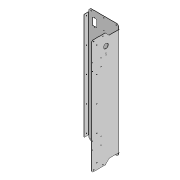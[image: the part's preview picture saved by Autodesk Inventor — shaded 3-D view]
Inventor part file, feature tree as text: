
AUTODESK INVENTOR PART (.ipt)
format: ipt  version: 2020 (Build 240168000, 168)  size: 658,944 bytes
history: native  units: mm
features: sketch x20, projected_geometry x12, other x10, hole x10, extrude x7, fillet x5, chamfer x3
ambient origin geometry x8: Origin, YZ Plane, XZ Plane, XY Plane, X Axis, Y Axis, Z Axis, Center Point
bodies: Body1 (feature_tree)
feature tree (67):
  other  "ソリッド1"
  other  "フランジ1"
  extrude  "押し出し2"  Depth=200.0mm
  hole  "穴2"  [1 undecoded]
  fillet  "フィレット1"  Radius=2.0mm
  other  "フランジ3"
  hole  "穴4"  [1 undecoded]
  hole  "穴5"  [1 undecoded]
  hole  "穴6"  [1 undecoded]
  hole  "穴7"  [1 undecoded]
  extrude  "押し出し3"  Depth=30.0mm TaperAngle=90.0deg
  hole  "穴8"  [1 undecoded]
  hole  "穴9"  [1 undecoded]
  extrude  "押し出し4"  Depth=2.0mm
  hole  "穴10"  [1 undecoded]
  chamfer  "面取り1"  Distance=47.0mm
  fillet  "フィレット2"  Radius=10.0mm
  extrude  "押し出し5"  Depth=20.594885mm
  hole  "穴11"  [1 undecoded]
  chamfer  "面取り2"  Distance=2.0mm
  chamfer  "面取り3"  Distance=1.0mm
  fillet  "フィレット3"  Radius=4.0mm
  extrude  "押し出し6"  Depth=2.0mm
  hole  "穴12"  [1 undecoded]
  extrude  "押し出し7"  Depth=8.0mm
  fillet  "フィレット4"  Radius=2.0mm
  extrude  "押し出し8"  Depth=2.0mm
  fillet  "フィレット5"  Radius=40.0mm
  sketch  "スケッチ1"
  other  "プレート1"
  sketch  "スケッチ2"
  other  "プレート2"
  other  "曲げ1"
  other  "コーナー1"
  sketch  "スケッチ6"
  sketch  "スケッチ7"
  projected_geometry  "投影ループ8"
  sketch  "スケッチ9"
  other  "プレート4"
  other  "曲げ3"
  other  "コーナー3"
  sketch  "スケッチ10"
  projected_geometry  "投影ループ9"
  sketch  "スケッチ11"
  projected_geometry  "投影ループ10"
  sketch  "スケッチ12"
  projected_geometry  "投影ループ11"
  sketch  "スケッチ13"
  sketch  "スケッチ14"
  projected_geometry  "投影ループ12"
  sketch  "スケッチ15"
  projected_geometry  "投影ループ13"
  sketch  "スケッチ16"
  projected_geometry  "投影ループ14"
  sketch  "スケッチ17"
  sketch  "スケッチ18"
  projected_geometry  "投影ループ15"
  sketch  "スケッチ19"
  sketch  "スケッチ20"
  projected_geometry  "投影ループ16"
  sketch  "スケッチ21"
  sketch  "スケッチ22"
  projected_geometry  "投影ループ17"
  sketch  "スケッチ23"
  projected_geometry  "投影ループ18"
  sketch  "スケッチ24"
  projected_geometry  "投影ループ19"
note: 10 required parameter values undecoded (feature->parameter linkage not recoverable at this tier; creation-order binding heuristic only, values carry confidence <= 0.55)
